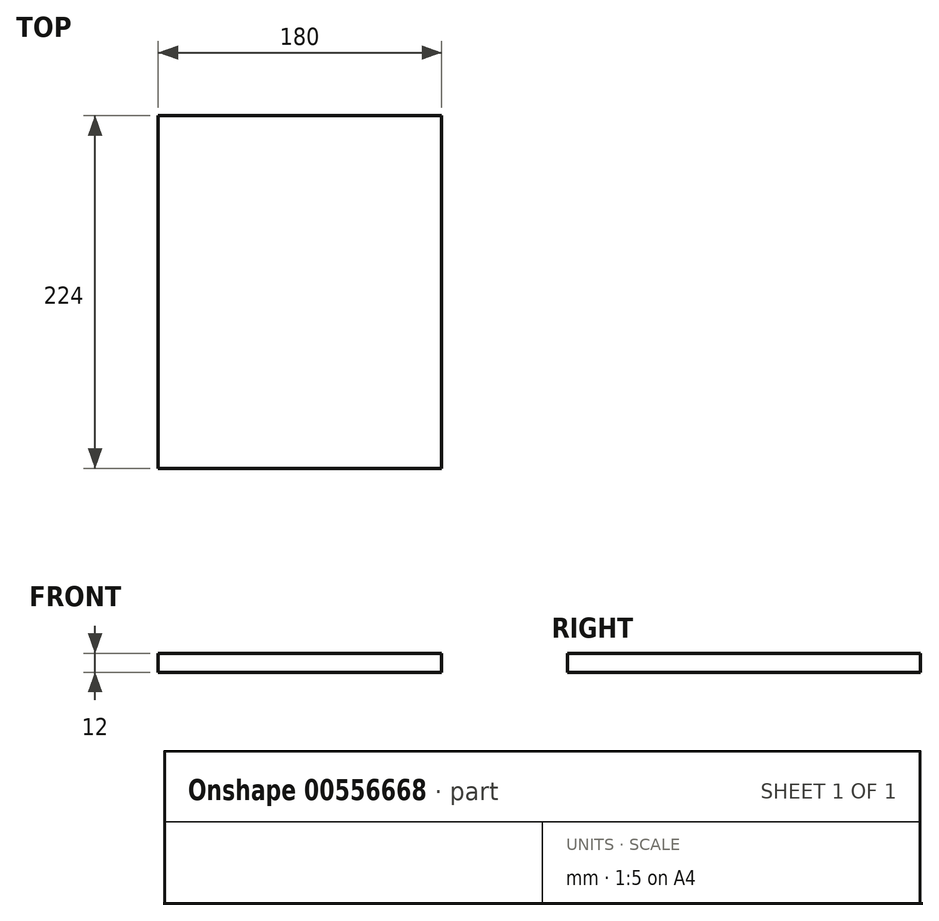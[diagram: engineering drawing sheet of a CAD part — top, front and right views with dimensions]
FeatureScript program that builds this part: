
annotation { "Feature Type Name" : "Feature", "Feature Type Description" : "" }
export const myFeature = defineFeature(function(context is Context, id is Id, definition is map)
    precondition{}
    {
        {
            var Q0;
            Q0=qCreatedBy(makeId("Top.planeOp"),FACE);
            var sketch = newSketch(context, id + "F0", { "sketchPlane" : qUnion([Q0])});
            skLineSegment(sketch, "E0", {"start": v(0, 0) * mm, "end": v(0, -224) * mm});
            skLineSegment(sketch, "E1", {"start": v(0, -224) * mm, "end": v(180, -224) * mm});
            skLineSegment(sketch, "E2", {"start": v(180, -224) * mm, "end": v(180, 0) * mm});
            skLineSegment(sketch, "E3", {"start": v(180, 0) * mm, "end": v(0, 0) * mm});
            skSolve(sketch);
        }
        {
            var Q0;
            Q0=makeQuery(id+"F0.imprint","IMPRINT",FACE,{"disambiguationData":[TD([[makeQuery(id+"F0.imprint","IMPRINT",EDGE,{"derivedFrom":sQuery(id+"F0.wireOp",EDGE,"E0")}),1.0]])]});
            extrude(context, id + "F1", {"entities" : qUnion([Q0]), "depth" : 12 * mm, "offsetDistance" : 25 * mm});
        }
    });
